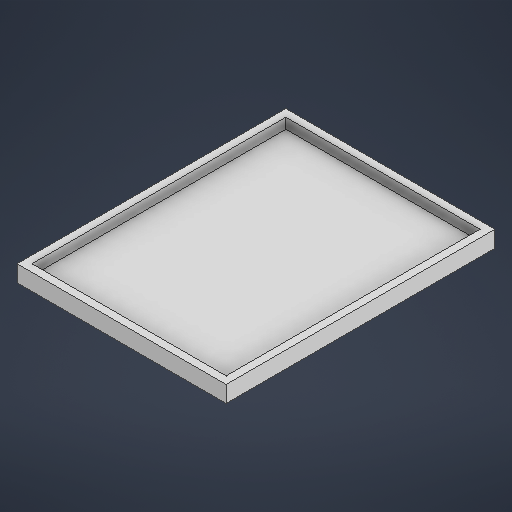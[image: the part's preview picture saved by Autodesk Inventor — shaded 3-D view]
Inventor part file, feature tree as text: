
AUTODESK INVENTOR PART (.ipt)
format: ipt  version: 2025 (Build 290162010, 162A)  size: 200,704 bytes
history: native  units: mm
features: extrude x2, sketch x1
ambient origin geometry x8: Origin, YZ Plane, XZ Plane, XY Plane, X Axis, Y Axis, Z Axis, Center Point
bodies: Solid1 (feature_tree)
feature tree (3):
  sketch  "Sketch1"  dims[d0=65.0mm d1=85.0mm d6=70.0mm d7=90.0mm d8=2.0mm d9=0.0mm d10=5.5mm d11=0.0mm]
  extrude  "Extrusion1"  Depth=85.0mm
  extrude  "Extrusion2"  Depth=70.0mm
